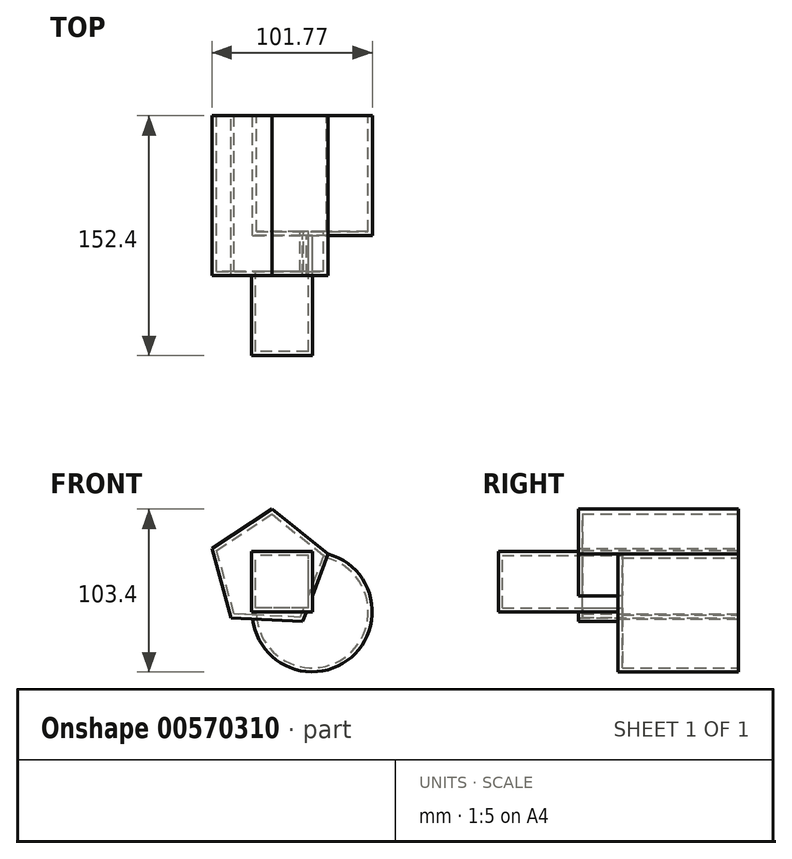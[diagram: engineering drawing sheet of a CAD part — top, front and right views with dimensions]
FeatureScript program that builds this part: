
annotation { "Feature Type Name" : "Feature", "Feature Type Description" : "" }
export const myFeature = defineFeature(function(context is Context, id is Id, definition is map)
    precondition{}
    {
        {
            var Q0;
            Q0=qCreatedBy(makeId("Front.planeOp"),FACE);
            var sketch = newSketch(context, id + "F0", { "sketchPlane" : qUnion([Q0])});
            skCircle(sketch, "E0", {"center": v(0, 0) * mm, "radius": 38.1 * mm});
            skLineSegment(sketch, "E1.bottom", {"start": v(0, 0) * mm, "end": v(-38.42, 0) * mm});
            skLineSegment(sketch, "E1.top", {"start": v(0, 38.42) * mm, "end": v(-38.42, 38.42) * mm});
            skLineSegment(sketch, "E1.left", {"start": v(0, 0) * mm, "end": v(0, 38.42) * mm});
            skLineSegment(sketch, "E1.right", {"start": v(-38.42, 0) * mm, "end": v(-38.42, 38.42) * mm});
            skCircle(sketch, "E2.cCircle", {"center": v(-27.36, 26.5) * mm, "radius": 38.84 * mm, "construction": true});
            skLineSegment(sketch, "E2.0", {"start": v(10.12, 36.72) * mm, "end": v(-6.06, -5.98) * mm});
            skLineSegment(sketch, "E2.1", {"start": v(-6.06, -5.98) * mm, "end": v(-51.67, -3.79) * mm});
            skLineSegment(sketch, "E2.2", {"start": v(-51.67, -3.79) * mm, "end": v(-63.68, 40.27) * mm});
            skLineSegment(sketch, "E2.3", {"start": v(-63.68, 40.27) * mm, "end": v(-25.5, 65.3) * mm});
            skLineSegment(sketch, "E2.4", {"start": v(-25.5, 65.3) * mm, "end": v(10.12, 36.72) * mm});
            skSolve(sketch);
        }
        {
            var Q0;
            {var subQ0=sQuery(id+"F0.wireOp",EDGE,"E1.left");var subQ1=sQuery(id+"F0.wireOp",EDGE,"E0");var subQ2=makeQuery(id+"F0.imprint","INTERSECT",VERTEX,{"derivedFrom":[subQ1,subQ0]});Q0=makeQuery(id+"F0.imprint","IMPRINT",FACE,{"disambiguationData":[TD([[makeQuery(id+"F0.imprint","IMPRINT",EDGE,{"disambiguationData":[TD([[subQ2,-1.0]])],"derivedFrom":subQ1}),1.0]])]});}
            var Q1;
            {var subQ1=sQuery(id+"F0.wireOp",EDGE,"E1.top");Q1=makeQuery(id+"F0.imprint","IMPRINT",FACE,{"disambiguationData":[TD([[makeQuery(id+"F0.imprint","IMPRINT",EDGE,{"derivedFrom":subQ1}),1.0]])]});}
            var Q2;
            {var subQ0=sQuery(id+"F0.wireOp",EDGE,"E1.left");var subQ1=sQuery(id+"F0.wireOp",EDGE,"E1.bottom");var subQ2=makeQuery(id+"F0.imprint","INTERSECT",VERTEX,{"derivedFrom":[subQ1,subQ0]});Q2=makeQuery(id+"F0.imprint","IMPRINT",FACE,{"disambiguationData":[TD([[makeQuery(id+"F0.imprint","IMPRINT",EDGE,{"disambiguationData":[TD([[subQ2,-1.0]])],"derivedFrom":subQ1}),-1.0]])]});}
            extrude(context, id + "F1", {"entities" : qUnion([Q0, Q1, Q2]), "depth" : 152.4 * mm, "offsetDistance" : 25.4 * mm});
        }
        {
            var Q0;
            {var subQ3=sQuery(id+"F0.wireOp",EDGE,"E1.left");var subQ5=sQuery(id+"F0.wireOp",EDGE,"E1.bottom");var subQ6=makeQuery(id+"F0.imprint","INTERSECT",VERTEX,{"derivedFrom":[subQ5,subQ3]});Q0=makeQuery(id+"F0.imprint","IMPRINT",FACE,{"disambiguationData":[TD([[makeQuery(id+"F0.imprint","IMPRINT",EDGE,{"disambiguationData":[TD([[subQ6,-1.0]])],"derivedFrom":subQ5}),1.0]])]});}
            extrude(context, id + "F2", {"entities" : qUnion([Q0]), "operationType" : NewBodyOperationType.ADD, "depth" : 76.2 * mm, "offsetDistance" : 25.4 * mm});
        }
        {
            var Q0;
            {var subQ5=sQuery(id+"F0.wireOp",EDGE,"E1.top");Q0=makeQuery(id+"F0.imprint","IMPRINT",FACE,{"disambiguationData":[TD([[makeQuery(id+"F0.imprint","IMPRINT",EDGE,{"derivedFrom":subQ5}),-1.0]])]});}
            var Q1;
            {var subQ0=sQuery(id+"F0.wireOp",EDGE,"E2.1");var subQ1=sQuery(id+"F0.wireOp",EDGE,"E0");var subQ2=makeQuery(id+"F0.imprint","INTERSECT",VERTEX,{"derivedFrom":[subQ1,subQ0]});Q1=makeQuery(id+"F0.imprint","IMPRINT",FACE,{"disambiguationData":[TD([[makeQuery(id+"F0.imprint","IMPRINT",EDGE,{"disambiguationData":[TD([[subQ2,1.0]])],"derivedFrom":subQ1}),1.0]])]});}
            var Q2;
            {var subQ1=sQuery(id+"F0.wireOp",EDGE,"E0");var subQ3=sQuery(id+"F0.wireOp",EDGE,"E1.left");var subQ4=makeQuery(id+"F0.imprint","INTERSECT",VERTEX,{"derivedFrom":[subQ1,subQ3]});Q2=makeQuery(id+"F0.imprint","IMPRINT",FACE,{"disambiguationData":[TD([[makeQuery(id+"F0.imprint","IMPRINT",EDGE,{"disambiguationData":[TD([[subQ4,1.0]])],"derivedFrom":subQ3}),-1.0]])]});}
            extrude(context, id + "F3", {"entities" : qUnion([Q0, Q1, Q2]), "operationType" : NewBodyOperationType.ADD, "depth" : 101.6 * mm, "offsetDistance" : 25.4 * mm});
        }
        {
            var Q0;
            {var subQ0=sQuery(id+"F0.wireOp",EDGE,"E2.1");var subQ1=sQuery(id+"F0.wireOp",EDGE,"E2.0");var subQ2=sQuery(id+"F0.wireOp",EDGE,"E1.right");var subQ3=sQuery(id+"F0.wireOp",EDGE,"E1.left");var subQ4=sQuery(id+"F0.wireOp",EDGE,"E1.top");var subQ5=sQuery(id+"F0.wireOp",EDGE,"E1.bottom");Q0=makeQuery(id+"F3.boolean.opBoolean","MERGE",FACE,{"derivedFrom":[makeQuery(id+"F2.boolean.opBoolean","MERGE",FACE,{"derivedFrom":[makeQuery(id+"F1.opExtrude","CAP_FACE",FACE,{"disambiguationData":[OSD([subQ5,subQ4,subQ3,subQ2])],"isStart":true}),makeQuery(id+"F2.opExtrude","CAP_FACE",FACE,{"disambiguationData":[OSD([sQuery(id+"F0.wireOp",EDGE,"E0"),subQ5,subQ3,subQ1,subQ0])],"isStart":true})]}),makeQuery(id+"F3.opExtrude","CAP_FACE",FACE,{"disambiguationData":[OSD([subQ5,subQ4,subQ3,subQ2,subQ1,subQ0,sQuery(id+"F0.wireOp",EDGE,"E2.2"),sQuery(id+"F0.wireOp",EDGE,"E2.3"),sQuery(id+"F0.wireOp",EDGE,"E2.4")])],"isStart":true})]});}
            shell(context, id + "F4", {"entities" : qUnion([Q0]), "thickness" : 2.54 * mm});
        }
    });
